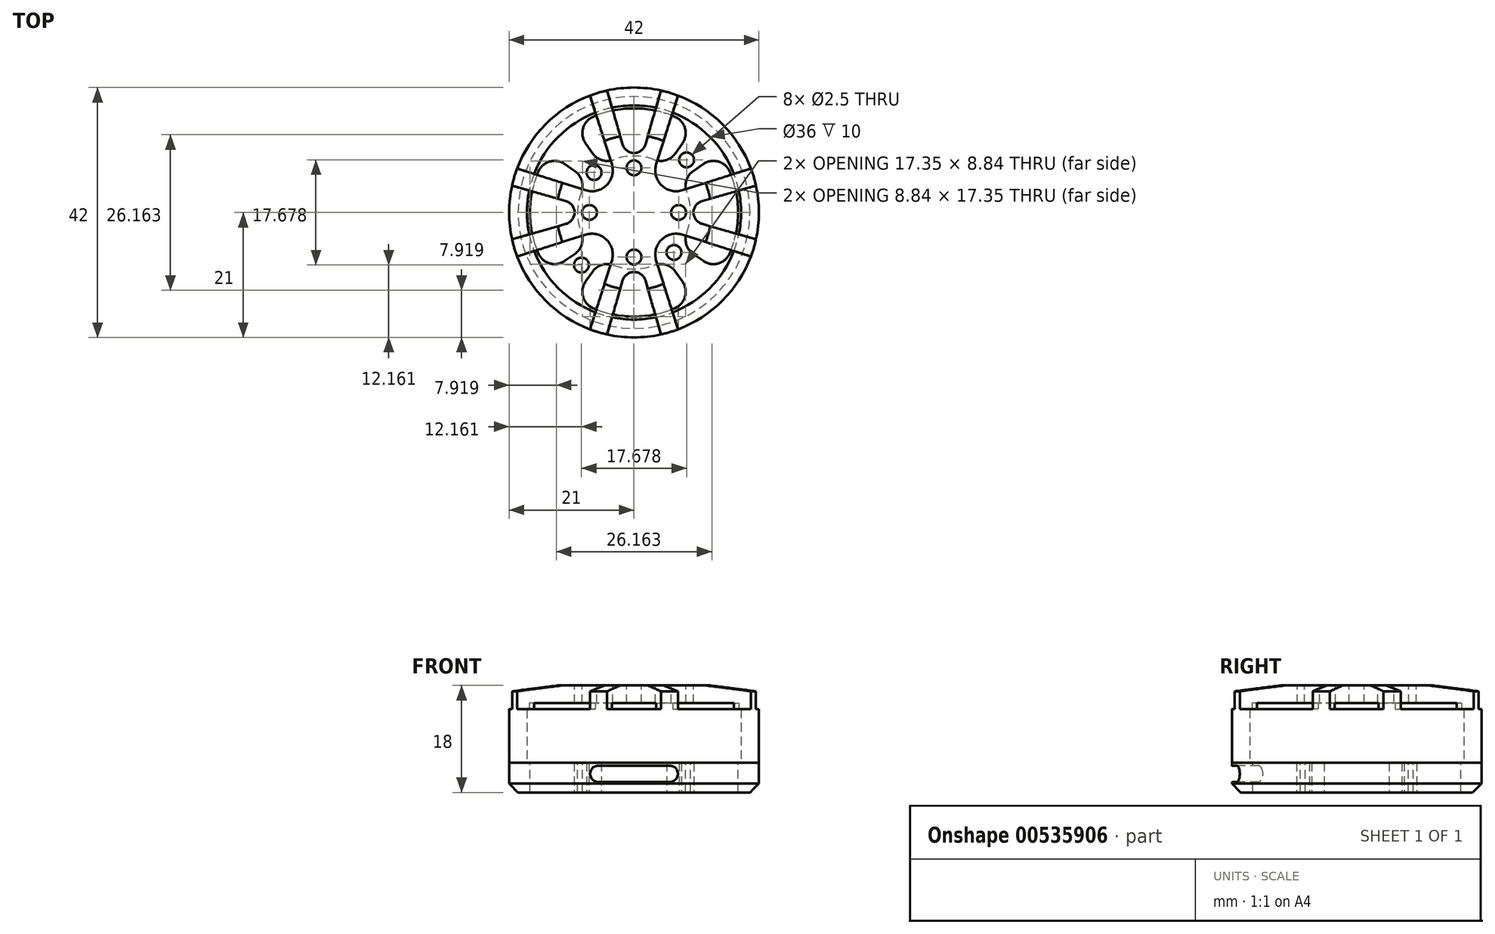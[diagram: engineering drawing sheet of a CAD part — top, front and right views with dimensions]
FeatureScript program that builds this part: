
annotation { "Feature Type Name" : "Feature", "Feature Type Description" : "" }
export const myFeature = defineFeature(function(context is Context, id is Id, definition is map)
    precondition{}
    {
        {
            var Q0;
            Q0=qCreatedBy(makeId("Top.planeOp"),FACE);
            var sketch = newSketch(context, id + "F0", { "sketchPlane" : qUnion([Q0])});
            skCircle(sketch, "E0", {"center": v(0, 0) * mm, "radius": 21 * mm});
            skSolve(sketch);
        }
        {
            var Q0;
            Q0 = qSketchRegion(id + "F0", true);
            extrude(context, id + "F1", {"entities" : qUnion([Q0]), "oppositeDirection" : true, "depth" : 5 * mm, "offsetDistance" : 25 * mm});
        }
        {
            var Q0;
            Q0=makeQuery(id+"F1.opExtrude","CAP_FACE",FACE,{"disambiguationData":[OSD([sQuery(id+"F0.wireOp",EDGE,"E0")])],"isStart":true});
            var sketch = newSketch(context, id + "F2", { "sketchPlane" : qUnion([Q0])});
            skArc(sketch, "E1", {"start": v(3.42, 8.86) * mm, "mid": v(0, 9.5) * mm, "end": v(-3.42, 8.86) * mm});
            skLineSegment(sketch, "E2", {"start": v(0, 21) * mm, "end": v(0, -21) * mm, "construction": true});
            skArc(sketch, "E3", {"start": v(6.85, 16.1) * mm, "mid": v(0, 17.5) * mm, "end": v(-6.85, 16.1) * mm});
            skLineSegment(sketch, "E4", {"start": v(-8.14, 11.62) * mm, "end": v(-6.96, 9.94) * mm});
            skLineSegment(sketch, "E5", {"start": v(8.14, 11.62) * mm, "end": v(6.96, 9.94) * mm});
            skPoint(sketch, "E6.visualSharp", {"position": v(-5.45, 7.78) * mm});
            skArc(sketch, "E6.filletArc", {"start": v(-6.96, 9.94) * mm, "mid": v(-5.38, 8.8) * mm, "end": v(-3.42, 8.86) * mm});
            skPoint(sketch, "E7.visualSharp", {"position": v(5.45, 7.78) * mm});
            skArc(sketch, "E7.filletArc", {"start": v(3.42, 8.86) * mm, "mid": v(5.38, 8.8) * mm, "end": v(6.96, 9.94) * mm});
            skPoint(sketch, "E8.visualSharp", {"position": v(10.04, 14.34) * mm});
            skArc(sketch, "E8.filletArc", {"start": v(8.14, 11.62) * mm, "mid": v(8.56, 14.17) * mm, "end": v(6.85, 16.1) * mm});
            skPoint(sketch, "E9.visualSharp", {"position": v(-10.04, 14.34) * mm});
            skArc(sketch, "E9.filletArc", {"start": v(-6.85, 16.1) * mm, "mid": v(-8.56, 14.17) * mm, "end": v(-8.14, 11.62) * mm});
            skArc(sketch, "E10.1.0", {"start": v(-16.1, 6.85) * mm, "mid": v(-17.5, 0) * mm, "end": v(-16.1, -6.85) * mm});
            skArc(sketch, "E10.1.1", {"start": v(-16.1, -6.85) * mm, "mid": v(-14.17, -8.56) * mm, "end": v(-11.62, -8.14) * mm});
            skLineSegment(sketch, "E10.1.2", {"start": v(-11.62, -8.14) * mm, "end": v(-9.94, -6.96) * mm});
            skArc(sketch, "E10.1.3", {"start": v(-9.94, -6.96) * mm, "mid": v(-8.8, -5.38) * mm, "end": v(-8.86, -3.42) * mm});
            skArc(sketch, "E10.1.4", {"start": v(-8.86, 3.42) * mm, "mid": v(-9.5, 0) * mm, "end": v(-8.86, -3.42) * mm});
            skArc(sketch, "E10.1.5", {"start": v(-8.86, 3.42) * mm, "mid": v(-8.8, 5.38) * mm, "end": v(-9.94, 6.96) * mm});
            skLineSegment(sketch, "E10.1.6", {"start": v(-11.62, 8.14) * mm, "end": v(-9.94, 6.96) * mm});
            skArc(sketch, "E10.1.7", {"start": v(-11.62, 8.14) * mm, "mid": v(-14.17, 8.56) * mm, "end": v(-16.1, 6.85) * mm});
            skArc(sketch, "E10.2.0", {"start": v(-6.85, -16.1) * mm, "mid": v(0, -17.5) * mm, "end": v(6.85, -16.1) * mm});
            skArc(sketch, "E10.2.1", {"start": v(6.85, -16.1) * mm, "mid": v(8.56, -14.17) * mm, "end": v(8.14, -11.62) * mm});
            skLineSegment(sketch, "E10.2.2", {"start": v(8.14, -11.62) * mm, "end": v(6.96, -9.94) * mm});
            skArc(sketch, "E10.2.3", {"start": v(6.96, -9.94) * mm, "mid": v(5.38, -8.8) * mm, "end": v(3.42, -8.86) * mm});
            skArc(sketch, "E10.2.4", {"start": v(-3.42, -8.86) * mm, "mid": v(0, -9.5) * mm, "end": v(3.42, -8.86) * mm});
            skArc(sketch, "E10.2.5", {"start": v(-3.42, -8.86) * mm, "mid": v(-5.38, -8.8) * mm, "end": v(-6.96, -9.94) * mm});
            skLineSegment(sketch, "E10.2.6", {"start": v(-8.14, -11.62) * mm, "end": v(-6.96, -9.94) * mm});
            skArc(sketch, "E10.2.7", {"start": v(-8.14, -11.62) * mm, "mid": v(-8.56, -14.17) * mm, "end": v(-6.85, -16.1) * mm});
            skArc(sketch, "E10.3.0", {"start": v(16.1, -6.85) * mm, "mid": v(17.5, 0) * mm, "end": v(16.1, 6.85) * mm});
            skArc(sketch, "E10.3.1", {"start": v(16.1, 6.85) * mm, "mid": v(14.17, 8.56) * mm, "end": v(11.62, 8.14) * mm});
            skLineSegment(sketch, "E10.3.2", {"start": v(11.62, 8.14) * mm, "end": v(9.94, 6.96) * mm});
            skArc(sketch, "E10.3.3", {"start": v(9.94, 6.96) * mm, "mid": v(8.8, 5.38) * mm, "end": v(8.86, 3.42) * mm});
            skArc(sketch, "E10.3.4", {"start": v(8.86, -3.42) * mm, "mid": v(9.5, 0) * mm, "end": v(8.86, 3.42) * mm});
            skArc(sketch, "E10.3.5", {"start": v(8.86, -3.42) * mm, "mid": v(8.8, -5.38) * mm, "end": v(9.94, -6.96) * mm});
            skLineSegment(sketch, "E10.3.6", {"start": v(11.62, -8.14) * mm, "end": v(9.94, -6.96) * mm});
            skArc(sketch, "E10.3.7", {"start": v(11.62, -8.14) * mm, "mid": v(14.17, -8.56) * mm, "end": v(16.1, -6.85) * mm});
            skSolve(sketch);
        }
        {
            var Q0;
            Q0 = qSketchRegion(id + "F2", true);
            extrude(context, id + "F3", {"entities" : qUnion([Q0]), "operationType" : NewBodyOperationType.REMOVE, "endBound" : BoundingType.THROUGH_ALL, "oppositeDirection" : true, "depth" : 25 * mm, "offsetDistance" : 25 * mm});
        }
        {
            var Q0;
            Q0=makeQuery(id+"F1.opExtrude","CAP_EDGE",EDGE,{"disambiguationData":[OSD([sQuery(id+"F0.wireOp",EDGE,"E0")])],"isStart":false});
            chamfer(context, id + "F4", {"entities" : qUnion([Q0]), "width" : 1.5 * mm, "tangentPropagation" : true});
        }
        {
            var Q0;
            Q0=qCreatedBy(makeId("Front.planeOp"),FACE);
            cPlane(context, id + "F5", {"entities" : qUnion([Q0]), "cplaneType" : CPlaneType.OFFSET, "offset" : 25 * mm, "width" : 150 * mm, "height" : 150 * mm});
        }
        {
            var Q0;
            Q0=qCreatedBy(id+"F5.planeOp",FACE);
            var sketch = newSketch(context, id + "F6", { "sketchPlane" : qUnion([Q0])});
            skArc(sketch, "E11", {"start": v(-6, -0.5) * mm, "mid": v(-7.38, -1.88) * mm, "end": v(-6, -3.25) * mm});
            skArc(sketch, "E12", {"start": v(6, -3.25) * mm, "mid": v(7.38, -1.88) * mm, "end": v(6, -0.5) * mm});
            skLineSegment(sketch, "E13", {"start": v(0, 0) * mm, "end": v(0, -11.13) * mm, "construction": true});
            skLineSegment(sketch, "E14", {"start": v(-6, -0.5) * mm, "end": v(6, -0.5) * mm});
            skLineSegment(sketch, "E15", {"start": v(-6, -3.25) * mm, "end": v(6, -3.25) * mm});
            skSolve(sketch);
        }
        {
            var Q0;
            Q0 = qSketchRegion(id + "F6", true);
            extrude(context, id + "F7", {"entities" : qUnion([Q0]), "operationType" : NewBodyOperationType.REMOVE, "oppositeDirection" : true, "depth" : 10 * mm, "offsetDistance" : 25 * mm});
        }
        {
            var Q0;
            Q0 = qSketchRegion(id + "F0", true);
            extrude(context, id + "F8", {"entities" : qUnion([Q0]), "depth" : 13 * mm, "offsetDistance" : 25 * mm});
        }
        {
            var Q0;
            Q0=makeQuery(id+"F8.opExtrude","CAP_FACE",FACE,{"disambiguationData":[OSD([sQuery(id+"F0.wireOp",EDGE,"E0")])],"isStart":false});
            var sketch = newSketch(context, id + "F9", { "sketchPlane" : qUnion([Q0])});
            skLineSegment(sketch, "E16", {"start": v(0, 0) * mm, "end": v(0, 21) * mm, "construction": true});
            skArc(sketch, "E17", {"start": v(-1.92, 11.45) * mm, "mid": v(0, 10) * mm, "end": v(1.92, 11.45) * mm});
            skLineSegment(sketch, "E18", {"start": v(0, 0) * mm, "end": v(14.85, 14.85) * mm, "construction": true});
            skArc(sketch, "E19", {"start": v(3.74, 8.13) * mm, "mid": v(4.6, 4.6) * mm, "end": v(8.13, 3.74) * mm});
            skLineSegment(sketch, "E20", {"start": v(1.92, 11.45) * mm, "end": v(4.52, 20.5) * mm});
            skLineSegment(sketch, "E21", {"start": v(3.74, 8.13) * mm, "end": v(7.4, 19.65) * mm});
            skLineSegment(sketch, "E22.MirrorCS", {"start": v(-1.92, 11.45) * mm, "end": v(-4.52, 20.5) * mm});
            skLineSegment(sketch, "E23.MirrorCS", {"start": v(8.13, 3.74) * mm, "end": v(19.65, 7.4) * mm});
            skArc(sketch, "E24", {"start": v(19.65, 7.4) * mm, "mid": v(14.85, 14.85) * mm, "end": v(7.4, 19.65) * mm});
            skArc(sketch, "E25.trimOffspring", {"start": v(4.52, 20.5) * mm, "mid": v(0, 21) * mm, "end": v(-4.52, 20.5) * mm});
            skLineSegment(sketch, "E26.1.0", {"start": v(-11.45, -1.92) * mm, "end": v(-20.5, -4.52) * mm});
            skArc(sketch, "E26.1.1", {"start": v(-11.45, -1.92) * mm, "mid": v(-10, 0) * mm, "end": v(-11.45, 1.92) * mm});
            skLineSegment(sketch, "E26.1.2", {"start": v(-11.45, 1.92) * mm, "end": v(-20.5, 4.52) * mm});
            skArc(sketch, "E26.1.3", {"start": v(-20.5, 4.52) * mm, "mid": v(-21, 0) * mm, "end": v(-20.5, -4.52) * mm});
            skLineSegment(sketch, "E26.1.4", {"start": v(-8.13, 3.74) * mm, "end": v(-19.65, 7.4) * mm});
            skArc(sketch, "E26.1.5", {"start": v(-8.13, 3.74) * mm, "mid": v(-4.6, 4.6) * mm, "end": v(-3.74, 8.13) * mm});
            skLineSegment(sketch, "E26.1.6", {"start": v(-3.74, 8.13) * mm, "end": v(-7.4, 19.65) * mm});
            skArc(sketch, "E26.1.7", {"start": v(-7.4, 19.65) * mm, "mid": v(-14.85, 14.85) * mm, "end": v(-19.65, 7.4) * mm});
            skLineSegment(sketch, "E26.2.0", {"start": v(1.92, -11.45) * mm, "end": v(4.52, -20.5) * mm});
            skArc(sketch, "E26.2.1", {"start": v(1.92, -11.45) * mm, "mid": v(0, -10) * mm, "end": v(-1.92, -11.45) * mm});
            skLineSegment(sketch, "E26.2.2", {"start": v(-1.92, -11.45) * mm, "end": v(-4.52, -20.5) * mm});
            skArc(sketch, "E26.2.3", {"start": v(-4.52, -20.5) * mm, "mid": v(0, -21) * mm, "end": v(4.52, -20.5) * mm});
            skLineSegment(sketch, "E26.2.4", {"start": v(-3.74, -8.13) * mm, "end": v(-7.4, -19.65) * mm});
            skArc(sketch, "E26.2.5", {"start": v(-3.74, -8.13) * mm, "mid": v(-4.6, -4.6) * mm, "end": v(-8.13, -3.74) * mm});
            skLineSegment(sketch, "E26.2.6", {"start": v(-8.13, -3.74) * mm, "end": v(-19.65, -7.4) * mm});
            skArc(sketch, "E26.2.7", {"start": v(-19.65, -7.4) * mm, "mid": v(-14.85, -14.85) * mm, "end": v(-7.4, -19.65) * mm});
            skLineSegment(sketch, "E26.3.0", {"start": v(11.45, 1.92) * mm, "end": v(20.5, 4.52) * mm});
            skArc(sketch, "E26.3.1", {"start": v(11.45, 1.92) * mm, "mid": v(10, 0) * mm, "end": v(11.45, -1.92) * mm});
            skLineSegment(sketch, "E26.3.2", {"start": v(11.45, -1.92) * mm, "end": v(20.5, -4.52) * mm});
            skArc(sketch, "E26.3.3", {"start": v(20.5, -4.52) * mm, "mid": v(21, 0) * mm, "end": v(20.5, 4.52) * mm});
            skLineSegment(sketch, "E26.3.4", {"start": v(8.13, -3.74) * mm, "end": v(19.65, -7.4) * mm});
            skArc(sketch, "E26.3.5", {"start": v(8.13, -3.74) * mm, "mid": v(4.6, -4.6) * mm, "end": v(3.74, -8.13) * mm});
            skLineSegment(sketch, "E26.3.6", {"start": v(3.74, -8.13) * mm, "end": v(7.4, -19.65) * mm});
            skArc(sketch, "E26.3.7", {"start": v(7.4, -19.65) * mm, "mid": v(14.85, -14.85) * mm, "end": v(19.65, -7.4) * mm});
            skSolve(sketch);
        }
        {
            var Q0;
            Q0 = qSketchRegion(id + "F9", true);
            extrude(context, id + "F10", {"entities" : qUnion([Q0]), "operationType" : NewBodyOperationType.REMOVE, "oppositeDirection" : true, "depth" : 4 * mm, "offsetDistance" : 25 * mm});
        }
        {
            var Q0;
            {var subQ0=sQuery(id+"F0.wireOp",EDGE,"E0");Q0=makeQuery(id+"F10.boolean.opBoolean","SPLIT",EDGE,{"disambiguationData":[TD([makeQuery(id+"F10.opExtrude","SWEPT_FACE",FACE,{"disambiguationData":[OSD([sQuery(id+"F9.wireOp",EDGE,"E26.1.0")])]})])],"derivedFrom":makeQuery(id+"F8.opExtrude","CAP_EDGE",EDGE,{"disambiguationData":[OSD([subQ0])],"isStart":false})});}
            var Q1;
            {var subQ0=sQuery(id+"F0.wireOp",EDGE,"E0");Q1=makeQuery(id+"F10.boolean.opBoolean","SPLIT",EDGE,{"disambiguationData":[TD([makeQuery(id+"F10.opExtrude","SWEPT_FACE",FACE,{"disambiguationData":[OSD([sQuery(id+"F9.wireOp",EDGE,"E26.1.2")])]})])],"derivedFrom":makeQuery(id+"F8.opExtrude","CAP_EDGE",EDGE,{"disambiguationData":[OSD([subQ0])],"isStart":false})});}
            var Q2;
            {var subQ0=sQuery(id+"F0.wireOp",EDGE,"E0");Q2=makeQuery(id+"F10.boolean.opBoolean","SPLIT",EDGE,{"disambiguationData":[TD([makeQuery(id+"F10.opExtrude","SWEPT_FACE",FACE,{"disambiguationData":[OSD([sQuery(id+"F9.wireOp",EDGE,"E22.MirrorCS")])]})])],"derivedFrom":makeQuery(id+"F8.opExtrude","CAP_EDGE",EDGE,{"disambiguationData":[OSD([subQ0])],"isStart":false})});}
            var Q3;
            {var subQ0=sQuery(id+"F0.wireOp",EDGE,"E0");Q3=makeQuery(id+"F10.boolean.opBoolean","SPLIT",EDGE,{"disambiguationData":[TD([makeQuery(id+"F10.opExtrude","SWEPT_FACE",FACE,{"disambiguationData":[OSD([sQuery(id+"F9.wireOp",EDGE,"E20")])]})])],"derivedFrom":makeQuery(id+"F8.opExtrude","CAP_EDGE",EDGE,{"disambiguationData":[OSD([subQ0])],"isStart":false})});}
            var Q4;
            {var subQ0=sQuery(id+"F0.wireOp",EDGE,"E0");Q4=makeQuery(id+"F10.boolean.opBoolean","SPLIT",EDGE,{"disambiguationData":[TD([makeQuery(id+"F10.opExtrude","SWEPT_FACE",FACE,{"disambiguationData":[OSD([sQuery(id+"F9.wireOp",EDGE,"E23.MirrorCS")])]})])],"derivedFrom":makeQuery(id+"F8.opExtrude","CAP_EDGE",EDGE,{"disambiguationData":[OSD([subQ0])],"isStart":false})});}
            var Q5;
            {var subQ0=sQuery(id+"F0.wireOp",EDGE,"E0");Q5=makeQuery(id+"F10.boolean.opBoolean","SPLIT",EDGE,{"disambiguationData":[TD([makeQuery(id+"F10.opExtrude","SWEPT_FACE",FACE,{"disambiguationData":[OSD([sQuery(id+"F9.wireOp",EDGE,"E26.3.2")])]})])],"derivedFrom":makeQuery(id+"F8.opExtrude","CAP_EDGE",EDGE,{"disambiguationData":[OSD([subQ0])],"isStart":false})});}
            var Q6;
            {var subQ0=sQuery(id+"F0.wireOp",EDGE,"E0");Q6=makeQuery(id+"F10.boolean.opBoolean","SPLIT",EDGE,{"disambiguationData":[TD([makeQuery(id+"F10.opExtrude","SWEPT_FACE",FACE,{"disambiguationData":[OSD([sQuery(id+"F9.wireOp",EDGE,"E26.2.0")])]})])],"derivedFrom":makeQuery(id+"F8.opExtrude","CAP_EDGE",EDGE,{"disambiguationData":[OSD([subQ0])],"isStart":false})});}
            var Q7;
            {var subQ0=sQuery(id+"F0.wireOp",EDGE,"E0");Q7=makeQuery(id+"F10.boolean.opBoolean","SPLIT",EDGE,{"disambiguationData":[TD([makeQuery(id+"F10.opExtrude","SWEPT_FACE",FACE,{"disambiguationData":[OSD([sQuery(id+"F9.wireOp",EDGE,"E26.2.2")])]})])],"derivedFrom":makeQuery(id+"F8.opExtrude","CAP_EDGE",EDGE,{"disambiguationData":[OSD([subQ0])],"isStart":false})});}
            chamfer(context, id + "F11", {"entities" : qUnion([Q0, Q1, Q2, Q3, Q4, Q5, Q6, Q7]), "chamferType" : ChamferType.TWO_OFFSETS, "width1" : 1 * mm, "oppositeDirection" : true, "width2" : 8 * mm, "tangentPropagation" : true});
        }
        {
            var Q0;
            Q0=makeQuery(id+"F8.opExtrude","CAP_FACE",FACE,{"disambiguationData":[OSD([sQuery(id+"F0.wireOp",EDGE,"E0")])],"isStart":true});
            var sketch = newSketch(context, id + "F12", { "sketchPlane" : qUnion([Q0])});
            skCircle(sketch, "E27", {"center": v(0, 0) * mm, "radius": 18 * mm});
            skSolve(sketch);
        }
        {
            var Q0;
            Q0 = qSketchRegion(id + "F12", true);
            extrude(context, id + "F13", {"entities" : qUnion([Q0]), "operationType" : NewBodyOperationType.REMOVE, "oppositeDirection" : true, "depth" : 10 * mm, "offsetDistance" : 25 * mm});
        }
        {
            var Q0;
            Q0=makeQuery(id+"F8.opExtrude","CAP_FACE",FACE,{"disambiguationData":[OSD([sQuery(id+"F0.wireOp",EDGE,"E0")])],"isStart":false});
            var sketch = newSketch(context, id + "F14", { "sketchPlane" : qUnion([Q0])});
            skCircle(sketch, "E28", {"center": v(0, 0) * mm, "radius": 7.5 * mm});
            skPoint(sketch, "E29", {"position": v(0, 7.5) * mm});
            skPoint(sketch, "E30", {"position": v(0, -7.5) * mm});
            skPoint(sketch, "E31", {"position": v(7.5, 0) * mm});
            skPoint(sketch, "E32", {"position": v(-7.5, 0) * mm});
            skSolve(sketch);
        }
        {
            var Q0;
            Q0=sQuery(id+"F14.wireOp",VERTEX,"E29");
            var Q1;
            Q1=sQuery(id+"F14.wireOp",VERTEX,"E31");
            var Q2;
            Q2=sQuery(id+"F14.wireOp",VERTEX,"E30");
            var Q3;
            Q3=sQuery(id+"F14.wireOp",VERTEX,"E32");
            var Q4;
            Q4=makeQuery(id+"F8.opExtrude","SWEPT_BODY",BODY,{"disambiguationData":[OSD([sQuery(id+"F0.wireOp",EDGE,"E0")])]});
            hole(context, id + "F15", {"style" : HoleStyle.SIMPLE, "endStyle" : HoleEndStyle.THROUGH, "standardTappedOrClearance" : lookupTablePath({ "standard" : "ISO", "engagement" : "75%", "pitch" : "0.5 mm", "size" : "M3", "type" : "Tapped" }), "standardBlindInLast" : lookupTablePath({ "standard" : "ISO", "engagement" : "75%", "pitch" : "0.5 mm", "size" : "M3", "type" : "Tapped" }), "holeDiameter" : 2.5 * mm, "showTappedDepth" : true, "isTappedThrough" : true, "tappedDepth" : 12 * mm, "tapClearance" : 3, "locations" : qUnion([Q0, Q1, Q2, Q3]), "scope" : qUnion([Q4]), "majorDiameter" : 3 * mm});
        }
        {
            var Q0;
            Q0=makeQuery(id+"F1.opExtrude","CAP_FACE",FACE,{"disambiguationData":[OSD([sQuery(id+"F0.wireOp",EDGE,"E0")])],"isStart":false});
            var sketch = newSketch(context, id + "F16", { "sketchPlane" : qUnion([Q0])});
            skCircle(sketch, "E33", {"center": v(0, 0) * mm, "radius": 12.5 * mm});
            skCircle(sketch, "E34", {"center": v(0, 0) * mm, "radius": 9.5 * mm});
            skLineSegment(sketch, "E35", {"start": v(-8.84, -8.84) * mm, "end": v(8.84, 8.84) * mm});
            skLineSegment(sketch, "E36", {"start": v(-8.84, 8.84) * mm, "end": v(8.84, -8.84) * mm});
            skLineSegment(sketch, "E37", {"start": v(0, 0) * mm, "end": v(-23.61, 0) * mm, "construction": true});
            skPoint(sketch, "E38", {"position": v(-8.84, 8.84) * mm});
            skPoint(sketch, "E39", {"position": v(8.84, -8.84) * mm});
            skPoint(sketch, "E40", {"position": v(-6.72, -6.72) * mm});
            skPoint(sketch, "E41", {"position": v(6.72, 6.72) * mm});
            skSolve(sketch);
        }
        {
            var Q0;
            Q0=sQuery(id+"F16.wireOp",VERTEX,"E40");
            var Q1;
            Q1=sQuery(id+"F16.wireOp",VERTEX,"E38");
            var Q2;
            Q2=sQuery(id+"F16.wireOp",VERTEX,"E41");
            var Q3;
            Q3=sQuery(id+"F16.wireOp",VERTEX,"E39");
            var Q4;
            Q4=makeQuery(id+"F1.opExtrude","SWEPT_BODY",BODY,{"disambiguationData":[OSD([sQuery(id+"F0.wireOp",EDGE,"E0")])]});
            hole(context, id + "F17", {"style" : HoleStyle.SIMPLE, "endStyle" : HoleEndStyle.THROUGH, "standardTappedOrClearance" : lookupTablePath({ "standard" : "ISO", "engagement" : "75%", "pitch" : "0.5 mm", "size" : "M3", "type" : "Tapped" }), "standardBlindInLast" : lookupTablePath({ "standard" : "ISO", "engagement" : "75%", "pitch" : "0.5 mm", "size" : "M3", "type" : "Tapped" }), "holeDiameter" : 2.5 * mm, "showTappedDepth" : true, "isTappedThrough" : true, "tappedDepth" : 12 * mm, "tapClearance" : 3, "locations" : qUnion([Q0, Q1, Q2, Q3]), "scope" : qUnion([Q4]), "majorDiameter" : 3 * mm});
        }
    });
